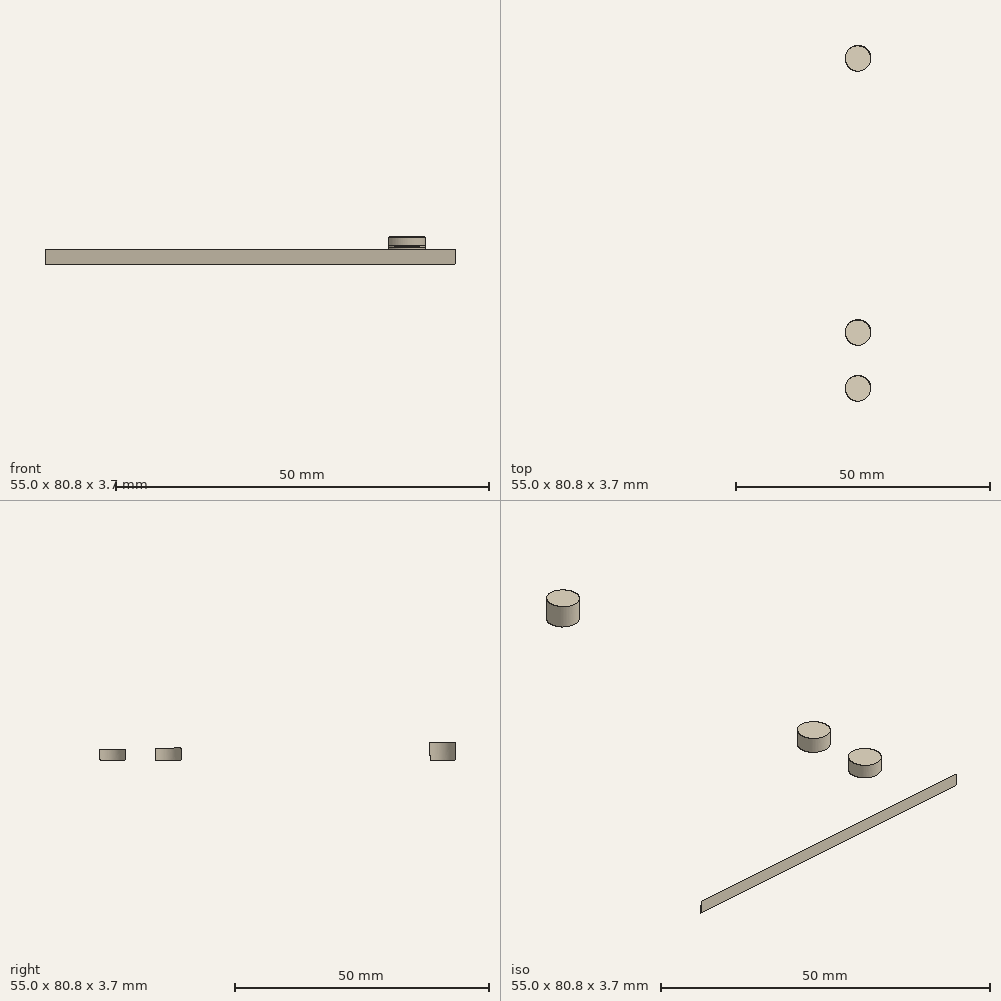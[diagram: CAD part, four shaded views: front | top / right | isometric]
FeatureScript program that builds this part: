
annotation { "Feature Type Name" : "Feature", "Feature Type Description" : "" }
export const myFeature = defineFeature(function(context is Context, id is Id, definition is map)
    precondition{}
    {
        {
            var Q0;
            Q0=qCreatedBy(makeId("Right.planeOp"),FACE);
            var sketch = newSketch(context, id + "F0", { "sketchPlane" : qUnion([Q0])});
            skLineSegment(sketch, "E0", {"start": v(13.78, -13.39) * mm, "end": v(-71.16, -15.17) * mm});
            skLineSegment(sketch, "E1", {"start": v(-71.16, -17.17) * mm, "end": v(13.84, -17.17) * mm});
            skLineSegment(sketch, "E2", {"start": v(-71.16, -15.17) * mm, "end": v(-71.16, -17.17) * mm});
            skLineSegment(sketch, "E3", {"start": v(13.78, -13.39) * mm, "end": v(13.84, -17.17) * mm});
            skSolve(sketch);
        }
        {
            var Q0;
            Q0=makeQuery(id+"F0.imprint","IMPRINT",FACE,{"disambiguationData":[TD([[makeQuery(id+"F0.imprint","IMPRINT",EDGE,{"derivedFrom":sQuery(id+"F0.wireOp",EDGE,"E0")}),1.0]])]});
            extrude(context, id + "F1", {"entities" : qUnion([Q0]), "endBound" : BoundingType.SYMMETRIC, "depth" : 55 * mm, "offsetDistance" : 25 * mm});
        }
        {
            var Q0;
            Q0=makeQuery(id+"F1.opExtrude","SWEPT_FACE",FACE,{"disambiguationData":[OSD([sQuery(id+"F0.wireOp",EDGE,"E0")])]});
            var sketch = newSketch(context, id + "F2", { "sketchPlane" : qUnion([Q0])});
            skCircle(sketch, "E4", {"center": v(-21, 6.73) * mm, "radius": 2.5 * mm});
            skCircle(sketch, "E5", {"center": v(-21, -47.27) * mm, "radius": 2.5 * mm});
            skCircle(sketch, "E6", {"center": v(-21, -58.27) * mm, "radius": 2.5 * mm});
            skCircle(sketch, "E7.MirrorC", {"center": v(21, -58.27) * mm, "radius": 2.5 * mm});
            skCircle(sketch, "E8.MirrorC", {"center": v(21, -47.27) * mm, "radius": 2.5 * mm});
            skCircle(sketch, "E9.MirrorC", {"center": v(21, 6.73) * mm, "radius": 2.5 * mm});
            skSolve(sketch);
        }
        {
            var Q0;
            Q0=makeQuery(id+"F2.imprint","IMPRINT",FACE,{"disambiguationData":[TD([[makeQuery(id+"F2.imprint","IMPRINT",EDGE,{"derivedFrom":sQuery(id+"F2.wireOp",EDGE,"E4")}),1.0]])]});
            var Q1;
            Q1=makeQuery(id+"F2.imprint","IMPRINT",FACE,{"disambiguationData":[TD([[makeQuery(id+"F2.imprint","IMPRINT",EDGE,{"derivedFrom":sQuery(id+"F2.wireOp",EDGE,"E9.MirrorC")}),-1.0]])]});
            var Q2;
            Q2=makeQuery(id+"F2.imprint","IMPRINT",FACE,{"disambiguationData":[TD([[makeQuery(id+"F2.imprint","IMPRINT",EDGE,{"derivedFrom":sQuery(id+"F2.wireOp",EDGE,"E5")}),1.0]])]});
            var Q3;
            Q3=makeQuery(id+"F2.imprint","IMPRINT",FACE,{"disambiguationData":[TD([[makeQuery(id+"F2.imprint","IMPRINT",EDGE,{"derivedFrom":sQuery(id+"F2.wireOp",EDGE,"E8.MirrorC")}),-1.0]])]});
            var Q4;
            Q4=makeQuery(id+"F2.imprint","IMPRINT",FACE,{"disambiguationData":[TD([[makeQuery(id+"F2.imprint","IMPRINT",EDGE,{"derivedFrom":sQuery(id+"F2.wireOp",EDGE,"E6")}),1.0]])]});
            var Q5;
            Q5=makeQuery(id+"F2.imprint","IMPRINT",FACE,{"disambiguationData":[TD([[makeQuery(id+"F2.imprint","IMPRINT",EDGE,{"derivedFrom":sQuery(id+"F2.wireOp",EDGE,"E7.MirrorC")}),-1.0]])]});
            extrude(context, id + "F3", {"entities" : qUnion([Q0, Q1, Q2, Q3, Q4, Q5]), "operationType" : NewBodyOperationType.REMOVE, "oppositeDirection" : true, "depth" : 25 * mm, "offsetDistance" : 25 * mm});
        }
    });
